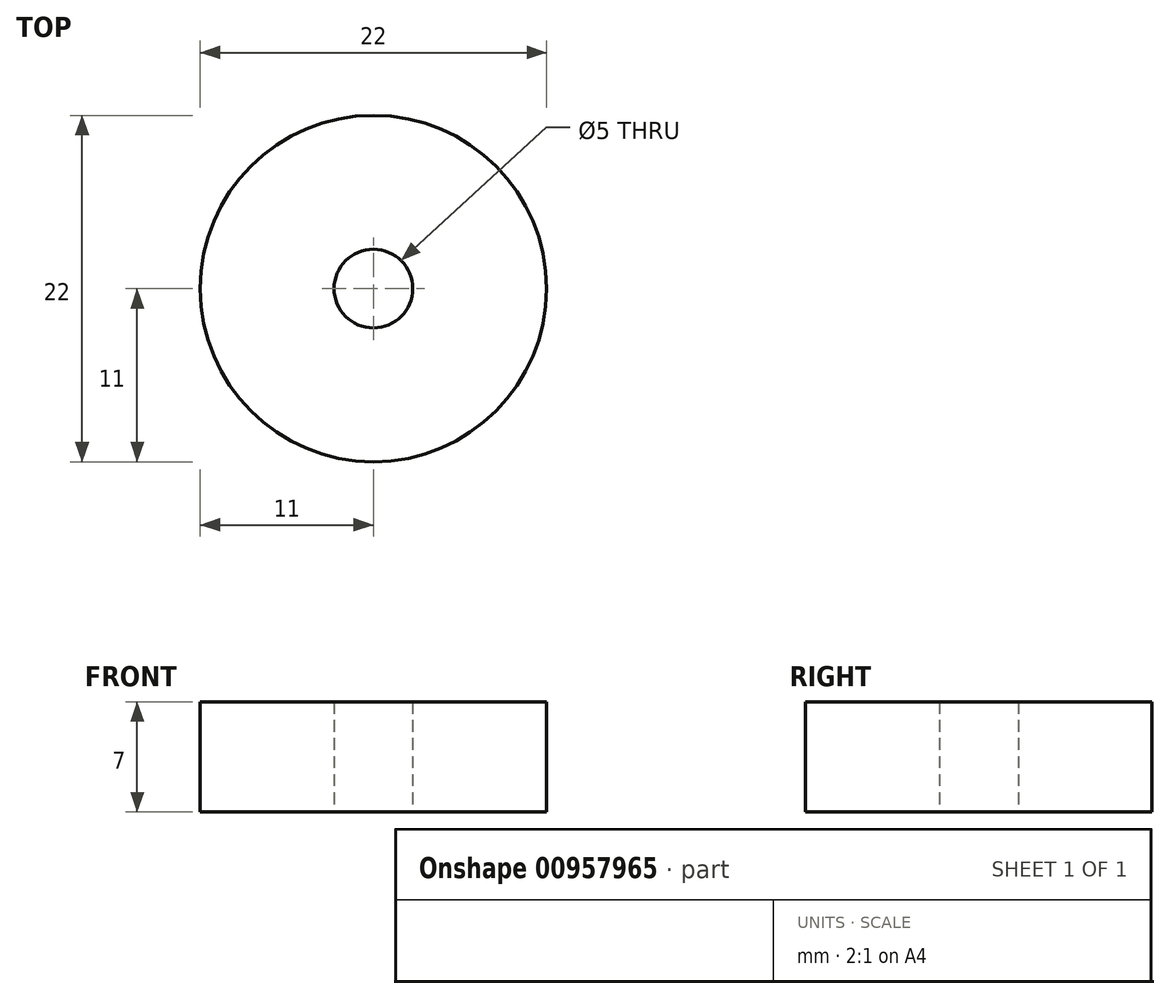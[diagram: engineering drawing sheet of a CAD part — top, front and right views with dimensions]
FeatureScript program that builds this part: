
annotation { "Feature Type Name" : "Feature", "Feature Type Description" : "" }
export const myFeature = defineFeature(function(context is Context, id is Id, definition is map)
    precondition{}
    {
        {
            var Q0;
            Q0=qCreatedBy(makeId("Top.planeOp"),FACE);
            var sketch = newSketch(context, id + "F0", { "sketchPlane" : qUnion([Q0])});
            skCircle(sketch, "E0", {"center": v(0, 0) * mm, "radius": 2.5 * mm});
            skCircle(sketch, "E1", {"center": v(0, 0) * mm, "radius": 11 * mm});
            skSolve(sketch);
        }
        {
            var Q0;
            Q0=makeQuery(id+"F0.imprint","IMPRINT",FACE,{"disambiguationData":[TD([[makeQuery(id+"F0.imprint","IMPRINT",EDGE,{"derivedFrom":sQuery(id+"F0.wireOp",EDGE,"E0")}),-1.0]])]});
            extrude(context, id + "F1", {"entities" : qUnion([Q0]), "depth" : 7 * mm, "offsetDistance" : 25 * mm});
        }
    });
